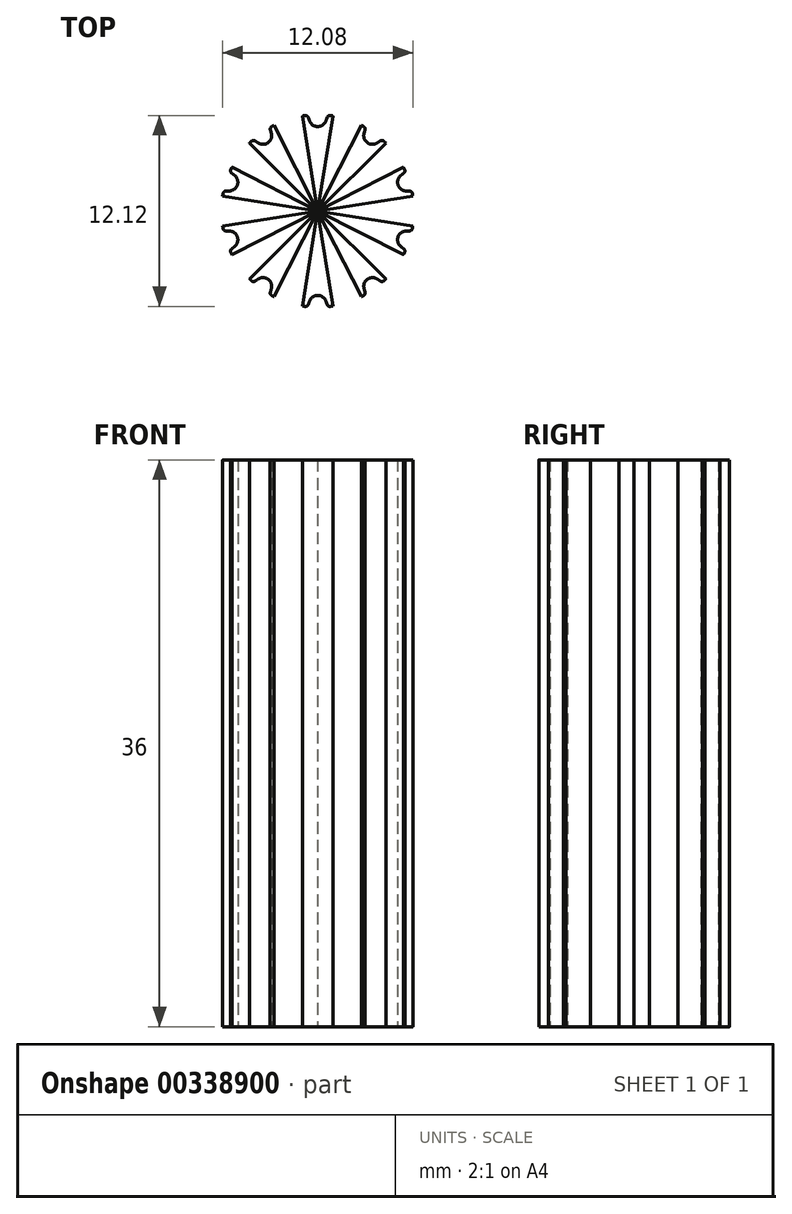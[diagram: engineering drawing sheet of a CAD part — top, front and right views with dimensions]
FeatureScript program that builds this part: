
annotation { "Feature Type Name" : "Feature", "Feature Type Description" : "" }
export const myFeature = defineFeature(function(context is Context, id is Id, definition is map)
    precondition{}
    {
        {
            assignVariable(context, id + "F0", {"name" : "teeth", "anyValue" : 10});
        }
        {
            assignVariable(context, id + "F1", {"name" : "total_length", "anyValue" : 36});
        }
        {
            var Q0;
            Q0=qCreatedBy(makeId("Top.planeOp"),FACE);
            var sketch = newSketch(context, id + "F2", { "sketchPlane" : qUnion([Q0])});
            skLineSegment(sketch, "E0", {"start": v(0, 0) * mm, "end": v(0, 5.36) * mm, "construction": true});
            skCircle(sketch, "E1", {"center": v(0, 0) * mm, "radius": 6.11 * mm});
            skPoint(sketch, "E2.MirrorCS.end.orphan", {"position": v(0.96, 6.04) * mm});
            skLineSegment(sketch, "E3", {"start": v(0.96, 6.04) * mm, "end": v(1, 6.29) * mm, "construction": true});
            skLineSegment(sketch, "E4", {"start": v(-0.96, 6.04) * mm, "end": v(-1, 6.29) * mm, "construction": true});
            skArc(sketch, "E5", {"start": v(0, 5.36) * mm, "mid": v(0.31, 5.46) * mm, "end": v(0.52, 5.72) * mm});
            skArc(sketch, "E6", {"start": v(0.52, 5.72) * mm, "mid": v(0.56, 5.83) * mm, "end": v(0.58, 5.94) * mm, "construction": true});
            skLineSegment(sketch, "E7", {"start": v(0, 5.36) * mm, "end": v(0, 6.11) * mm, "construction": true});
            skLineSegment(sketch, "E8", {"start": v(0, 6.11) * mm, "end": v(0, 6.37) * mm, "construction": true});
            skArc(sketch, "E9", {"start": v(0.58, 5.94) * mm, "mid": v(0.64, 6.04) * mm, "end": v(0.75, 6.07) * mm, "construction": true});
            skArc(sketch, "E10", {"start": v(1, 6.29) * mm, "mid": v(0, 6.37) * mm, "end": v(-1, 6.29) * mm, "construction": true});
            skLineSegment(sketch, "E11", {"start": v(0.96, 6.04) * mm, "end": v(0.84, 5.3) * mm});
            skLineSegment(sketch, "E12", {"start": v(0.84, 5.3) * mm, "end": v(0, 0) * mm});
            skLineSegment(sketch, "E13", {"start": v(0, 0) * mm, "end": v(-0.84, 5.3) * mm});
            skLineSegment(sketch, "E14", {"start": v(-0.84, 5.3) * mm, "end": v(-0.96, 6.04) * mm});
            skArc(sketch, "E15", {"start": v(0.8, 6.06) * mm, "mid": v(0.67, 6.03) * mm, "end": v(0.6, 5.93) * mm});
            skArc(sketch, "E16", {"start": v(0.52, 5.72) * mm, "mid": v(0.56, 5.83) * mm, "end": v(0.6, 5.93) * mm});
            skArc(sketch, "E17.MirrorCS", {"start": v(0, 5.36) * mm, "mid": v(-0.31, 5.46) * mm, "end": v(-0.52, 5.72) * mm});
            skArc(sketch, "E18.MirrorCS", {"start": v(-0.52, 5.72) * mm, "mid": v(-0.56, 5.83) * mm, "end": v(-0.6, 5.93) * mm});
            skArc(sketch, "E19.MirrorCS", {"start": v(-0.8, 6.06) * mm, "mid": v(-0.67, 6.03) * mm, "end": v(-0.6, 5.93) * mm});
            skArc(sketch, "E20", {"start": v(0, 6.11) * mm, "mid": v(-0.2, 6.1) * mm, "end": v(-0.4, 6.1) * mm});
            skArc(sketch, "E21", {"start": v(0.84, 5.3) * mm, "mid": v(0, 5.36) * mm, "end": v(-0.84, 5.3) * mm, "construction": true});
            skLineSegment(sketch, "E22", {"start": v(1, 6.29) * mm, "end": v(1.05, 6.66) * mm, "construction": true});
            skLineSegment(sketch, "E23", {"start": v(-1, 6.29) * mm, "end": v(-1.05, 6.66) * mm, "construction": true});
            skArc(sketch, "E24", {"start": v(-1.05, 6.66) * mm, "mid": v(0, 6.74) * mm, "end": v(1.05, 6.66) * mm, "construction": true});
            skSolve(sketch);
        }
        {
            var Q0;
            Q0=makeQuery(id+"F2.imprint","IMPRINT",FACE,{"disambiguationData":[TD([[makeQuery(id+"F2.imprint","IMPRINT",EDGE,{"derivedFrom":sQuery(id+"F2.wireOp",EDGE,"E5")}),-1.0]])]});
            var Q1;
            {var subQ1=sQuery(id+"F2.wireOp",EDGE,"E14");Q1=makeQuery(id+"F2.imprint","IMPRINT",FACE,{"disambiguationData":[TD([[makeQuery(id+"F2.imprint","IMPRINT",EDGE,{"derivedFrom":subQ1}),-1.0]])]});}
            var Q2;
            {var subQ0=sQuery(id+"F2.wireOp",EDGE,"E12");Q2=makeQuery(id+"F2.imprint","IMPRINT",FACE,{"disambiguationData":[TD([[makeQuery(id+"F2.imprint","IMPRINT",EDGE,{"derivedFrom":subQ0}),-1.0]])]});}
            extrude(context, id + "F3", {"entities" : qUnion([Q0, Q1, Q2]), "endBound" : BoundingType.SYMMETRIC, "depth" : (getVariable(context, 'total_length')) * mm});
        }
        {
            var Q0;
            Q0=makeQuery(id+"F3.opExtrude","SWEPT_BODY",BODY,{"disambiguationData":[OSD([sQuery(id+"F2.wireOp",EDGE,"E1"),sQuery(id+"F2.wireOp",EDGE,"E5"),sQuery(id+"F2.wireOp",EDGE,"E11"),sQuery(id+"F2.wireOp",EDGE,"E12"),sQuery(id+"F2.wireOp",EDGE,"E13"),sQuery(id+"F2.wireOp",EDGE,"E14"),sQuery(id+"F2.wireOp",EDGE,"E15"),sQuery(id+"F2.wireOp",EDGE,"E16"),sQuery(id+"F2.wireOp",EDGE,"E17.MirrorCS"),sQuery(id+"F2.wireOp",EDGE,"E18.MirrorCS"),sQuery(id+"F2.wireOp",EDGE,"E19.MirrorCS")])]});
            var Q1;
            Q1=makeQuery(id+"F3.opExtrude","SWEPT_EDGE",EDGE,{"disambiguationData":[OSD([sQuery(id+"F2.wireOp",EDGE,"E12"),sQuery(id+"F2.wireOp",EDGE,"E13")])]});
            circularPattern(context, id + "F4", {"operationType" : NewBodyOperationType.ADD, "entities" : qUnion([Q0]), "axis" : qUnion([Q1]), "angle" : 360 * degree, "instanceCount" : getVariable(context, 'teeth'), "equalSpace" : true});
        }
    });
